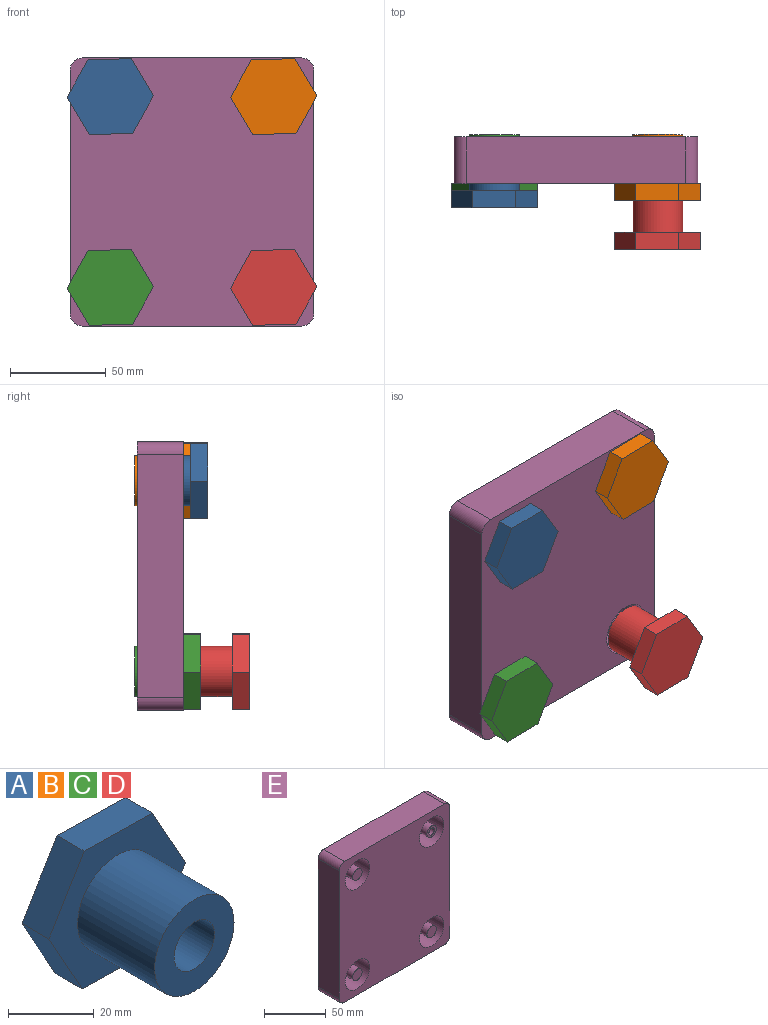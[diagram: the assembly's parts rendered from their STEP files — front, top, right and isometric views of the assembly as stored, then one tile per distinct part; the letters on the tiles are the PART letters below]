
ASSEMBLY  parts=5 mates=4
PART A: 12 faces, bbox 45x34.3x39.4 mm
  f0: cylinder r=6.65mm len=25.4mm, axis (0,1,0), area 1061.3mm2, adj f2,f11
  f1: cylinder r=13.08mm len=26.16mm, axis (0,1,0), area 2087.1mm2, adj f2,f3
  f2: plane 26.16x26.16mm, normal (0,-1,0), area 398.4mm2, adj f0,f1
  f3: plane 45.02x39.37mm, normal (0,-1,0), area 779.5mm2, adj f1,f5,f6,f7,f8,f9,f10
  f4: plane 45.02x39.37mm, normal (0,1,0), area 1316.8mm2, adj f5,f6,f7,f8,f9,f10
  f5: plane 19.3x11.58mm, normal (-0.86,0,0.51), area 200.1mm2, adj f3,f4,f6,f10
  f6: plane 22.51x8.89mm, normal (0.02,0,1), area 200.1mm2, adj f3,f4,f5,f7
  f7: plane 19.68x10.93mm, normal (0.87,0,0.49), area 200.1mm2, adj f3,f4,f6,f8
  f8: plane 19.3x11.58mm, normal (0.86,0,-0.51), area 200.1mm2, adj f3,f4,f7,f9
  f9: plane 22.51x8.89mm, normal (-0.02,0,-1), area 200.1mm2, adj f3,f4,f8,f10
  f10: plane 19.68x10.93mm, normal (-0.87,0,-0.49), area 200.1mm2, adj f3,f4,f5,f9
  f11: plane 13.3x13.3mm, normal (0,-1,0), area 138.9mm2, adj f0
PART B: same geometry as A
PART C: same geometry as A
PART D: same geometry as A
PART E: 28 faces, bbox 127x24.1x139.7 mm
  f0: plane 114.3x24.13mm, normal (0,0,-1), area 2758.1mm2, adj f1,f7,f12,f17
  f1: cylinder r=6.35mm len=24.13mm, axis (0,1,0), area 240.7mm2, adj f0,f2,f12,f17
  f2: plane 127x24.13mm, normal (1,0,0), area 3064.5mm2, adj f1,f3,f12,f17
  f3: cylinder r=6.35mm len=24.13mm, axis (0,1,0), area 240.7mm2, adj f2,f4,f12,f17
  f4: plane 114.3x24.13mm, normal (0,0,1), area 2758.1mm2, adj f3,f5,f12,f17
  f5: cylinder r=6.35mm len=24.13mm, axis (0,1,0), area 240.7mm2, adj f4,f6,f12,f17
  f6: plane 127x24.13mm, normal (-1,0,0), area 3064.5mm2, adj f5,f7,f12,f17
  f7: cylinder r=6.35mm len=24.13mm, axis (0,1,0), area 240.7mm2, adj f0,f6,f12,f17
  f8: cylinder r=13.99mm len=27.98mm, axis (0,1,0), area 1563.1mm2, adj f12,f14
  f9: cylinder r=13.99mm len=27.98mm, axis (0,1,0), area 1563.1mm2, adj f12,f15
  f10: cylinder r=13.99mm len=27.98mm, axis (0,1,0), area 1563.1mm2, adj f12,f16
  f11: cylinder r=13.99mm len=27.98mm, axis (0,1,0), area 1563.1mm2, adj f12,f13
  f12: plane 139.7x127mm, normal (0,-1,0), area 15247.1mm2, adj f0,f1,f2,f3,f4,f5,f6,f7
  f13: plane 27.98x27.98mm, normal (0,-1,0), area 522.6mm2, adj f11,f22
  f14: plane 27.98x27.98mm, normal (0,-1,0), area 522.6mm2, adj f8,f18
  f15: plane 27.98x27.98mm, normal (0,-1,0), area 522.6mm2, adj f9,f20
  f16: plane 27.98x27.98mm, normal (0,-1,0), area 522.6mm2, adj f10,f24
  f17: plane 139.7x127mm, normal (0,1,0), area 17707.3mm2, adj f0,f1,f2,f3,f4,f5,f6,f7
  f18: cylinder r=5.42mm len=17.78mm, axis (0,1,0), area 605.9mm2, adj f14,f19
  f19: plane 10.85x10.85mm, normal (0,-1,0), area 92.4mm2, adj f18
  f20: cylinder r=5.42mm len=17.78mm, axis (0,1,0), area 605.9mm2, adj f15,f21
  f21: plane 10.85x10.85mm, normal (0,-1,0), area 60.7mm2, adj f20,f26
  f22: cylinder r=5.42mm len=17.78mm, axis (0,1,0), area 605.9mm2, adj f13,f23
  f23: plane 10.85x10.85mm, normal (0,-1,0), area 92.4mm2, adj f22
  f24: cylinder r=5.42mm len=17.78mm, axis (0,1,0), area 605.9mm2, adj f16,f25
  f25: plane 10.85x10.85mm, normal (0,-1,0), area 92.4mm2, adj f24
  f26: cylinder r=3.17mm len=12.7mm, axis (0,-1,0), area 253.4mm2, adj f21,f27
  f27: cone r=0mm half-angle=59deg, axis (0,-1,0), area 36.9mm2, adj f26
PLACE A rot(axis=(1,0,0),180deg) t=(-81.39,-37.58,50.77)mm
PLACE B rot(axis=(1,0,0),180deg) t=(3.77,-33.77,50.77)mm
PLACE C rot(axis=(1,0,0),180deg) t=(-81.39,-33.77,-48.65)mm
PLACE D rot(axis=(1,0,0),180deg) t=(3.77,-59.17,-48.65)mm
PLACE E t=(-38.81,-15.99,1.06)mm fixed
MATE fastened E.f8 <-> E.f12  axis (0,-1,0) through (-81.39,-33.77,50.77)mm
MATE fastened D.f0 <-> E.f10  axis (0,1,0) through (3.77,-33.77,-48.65)mm
MATE fastened C.f0 <-> E.f11  axis (0,1,0) through (-81.39,-33.77,-48.65)mm
MATE fastened B.f0 <-> E.f9  axis (0,1,0) through (3.77,-33.77,50.77)mm
